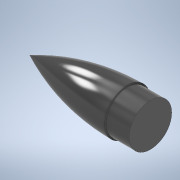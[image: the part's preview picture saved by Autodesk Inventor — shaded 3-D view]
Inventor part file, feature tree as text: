
AUTODESK INVENTOR PART (.ipt)
format: ipt  version: 2020 (Build 240168000, 168)  size: 156,672 bytes
history: native  units: mm
features: revolve x1, sketch x1
ambient origin geometry x8: Origin, YZ Plane, XZ Plane, XY Plane, X Axis, Y Axis, Z Axis, Center Point
bodies: Solid1 (feature_tree)
feature tree (2):
  revolve  "Revolution1"  [1 undecoded]
  sketch  "Sketch1"  dims[d1=39.5mm d2=40.0mm d3=37.0mm d4=2.0mm d5=2.0mm d6=90.0deg]
note: 1 required parameter value undecoded (feature->parameter linkage not recoverable at this tier; creation-order binding heuristic only, values carry confidence <= 0.55)
